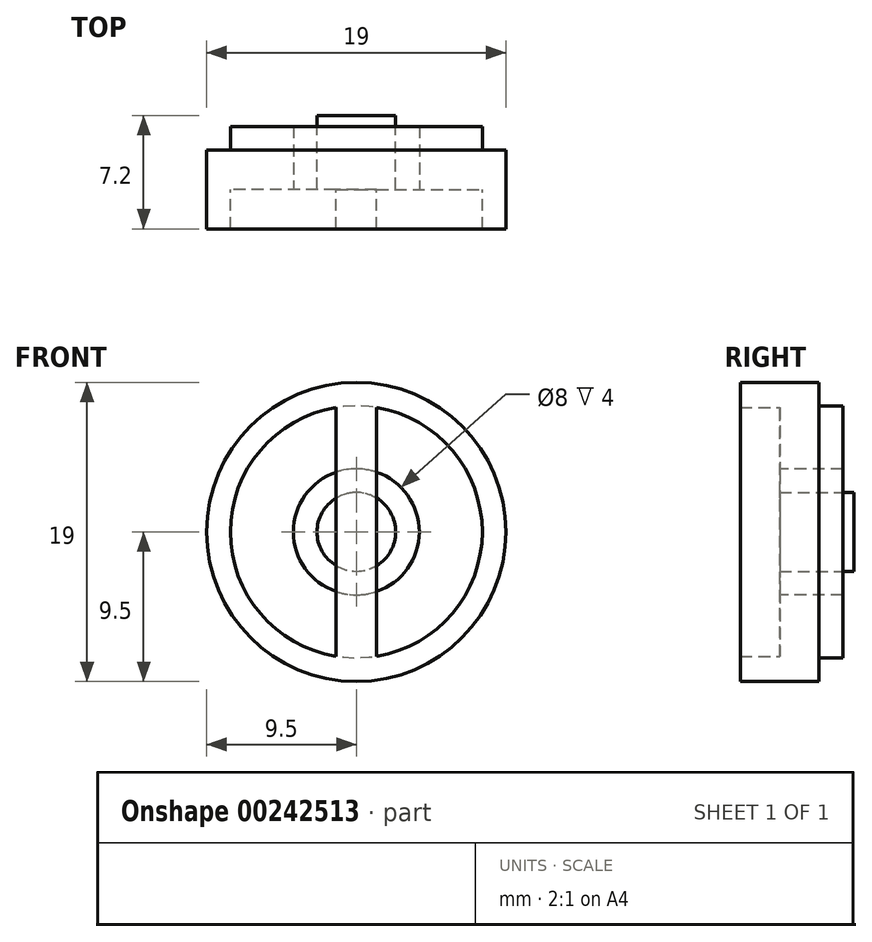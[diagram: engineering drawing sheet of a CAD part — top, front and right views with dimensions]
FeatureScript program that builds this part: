
annotation { "Feature Type Name" : "Feature", "Feature Type Description" : "" }
export const myFeature = defineFeature(function(context is Context, id is Id, definition is map)
    precondition{}
    {
        {
            var Q0;
            Q0=qCreatedBy(makeId("Front.planeOp"),FACE);
            var sketch = newSketch(context, id + "F0", { "sketchPlane" : qUnion([Q0])});
            skCircle(sketch, "E0", {"center": v(0, 0) * mm, "radius": 9.5 * mm});
            skCircle(sketch, "E1", {"center": v(0, 0) * mm, "radius": 8 * mm});
            skCircle(sketch, "E2", {"center": v(0, 0) * mm, "radius": 4 * mm});
            skSolve(sketch);
        }
        {
            var Q0;
            Q0 = qSketchRegion(id + "F0", true);
            extrude(context, id + "F1", {"entities" : qUnion([Q0]), "depth" : 5 * mm, "symmetric" : true});
        }
        {
            var Q0;
            Q0=qCreatedBy(makeId("Front.planeOp"),FACE);
            var sketch = newSketch(context, id + "F2", { "sketchPlane" : qUnion([Q0])});
            skLineSegment(sketch, "E3.bottom", {"start": v(-1.3, 8.33) * mm, "end": v(1.3, 8.33) * mm});
            skLineSegment(sketch, "E3.top", {"start": v(-1.3, -8.33) * mm, "end": v(1.3, -8.33) * mm});
            skLineSegment(sketch, "E3.left", {"start": v(-1.3, 8.33) * mm, "end": v(-1.3, -8.33) * mm});
            skLineSegment(sketch, "E3.right", {"start": v(1.3, 8.33) * mm, "end": v(1.3, -8.33) * mm});
            skPoint(sketch, "E3.middle", {"position": v(0, 0) * mm});
            skSolve(sketch);
        }
        {
            var Q0;
            Q0=makeQuery(id+"F2.imprint","IMPRINT",FACE,{"disambiguationData":[TD([[makeQuery(id+"F2.imprint","IMPRINT",EDGE,{"derivedFrom":sQuery(id+"F2.wireOp",EDGE,"E3.bottom")}),-1.0]])]});
            var Q1;
            Q1=makeQuery(id+"F1.opExtrude","CAP_FACE",FACE,{"disambiguationData":[OSD([sQuery(id+"F0.wireOp",EDGE,"E0"),sQuery(id+"F0.wireOp",EDGE,"E1")])],"isStart":true});
            extrude(context, id + "F3", {"entities" : qUnion([Q0, Q1]), "operationType" : NewBodyOperationType.ADD, "depth" : 2.5 * mm});
        }
        {
            var Q0;
            Q0=makeQuery(id+"F0.imprint","IMPRINT",FACE,{"disambiguationData":[TD([[makeQuery(id+"F0.imprint","IMPRINT",EDGE,{"derivedFrom":sQuery(id+"F0.wireOp",EDGE,"E1")}),1.0]])]});
            extrude(context, id + "F4", {"entities" : qUnion([Q0]), "operationType" : NewBodyOperationType.ADD, "oppositeDirection" : true, "depth" : 4 * mm});
        }
        {
            var Q0;
            Q0=makeQuery(id+"F3.opExtrude","CAP_FACE",FACE,{"disambiguationData":[OSD([sQuery(id+"F2.wireOp",EDGE,"E3.bottom"),sQuery(id+"F2.wireOp",EDGE,"E3.top"),sQuery(id+"F2.wireOp",EDGE,"E3.left"),sQuery(id+"F2.wireOp",EDGE,"E3.right")])],"isStart":true});
            cPlane(context, id + "F5", {"entities" : qUnion([Q0]), "cplaneType" : CPlaneType.OFFSET, "offset" : 25 * mm, "width" : 150 * mm, "height" : 150 * mm});
        }
        {
            var Q0;
            Q0=qCreatedBy(id+"F5.planeOp",FACE);
            var sketch = newSketch(context, id + "F6", { "sketchPlane" : qUnion([Q0])});
            skCircle(sketch, "E4", {"center": v(0, 0) * mm, "radius": 2.5 * mm});
            skSolve(sketch);
        }
        {
            var Q0;
            Q0=makeQuery(id+"F6.imprint","IMPRINT",FACE,{"disambiguationData":[TD([[makeQuery(id+"F6.imprint","IMPRINT",EDGE,{"derivedFrom":sQuery(id+"F6.wireOp",EDGE,"E4")}),1.0]])]});
            extrude(context, id + "F7", {"entities" : qUnion([Q0]), "operationType" : NewBodyOperationType.ADD, "oppositeDirection" : true, "depth" : 25 * mm, "hasSecondDirection" : true, "secondDirectionOppositeDirection" : true, "secondDirectionDepth" : 20.3 * mm});
        }
    });
